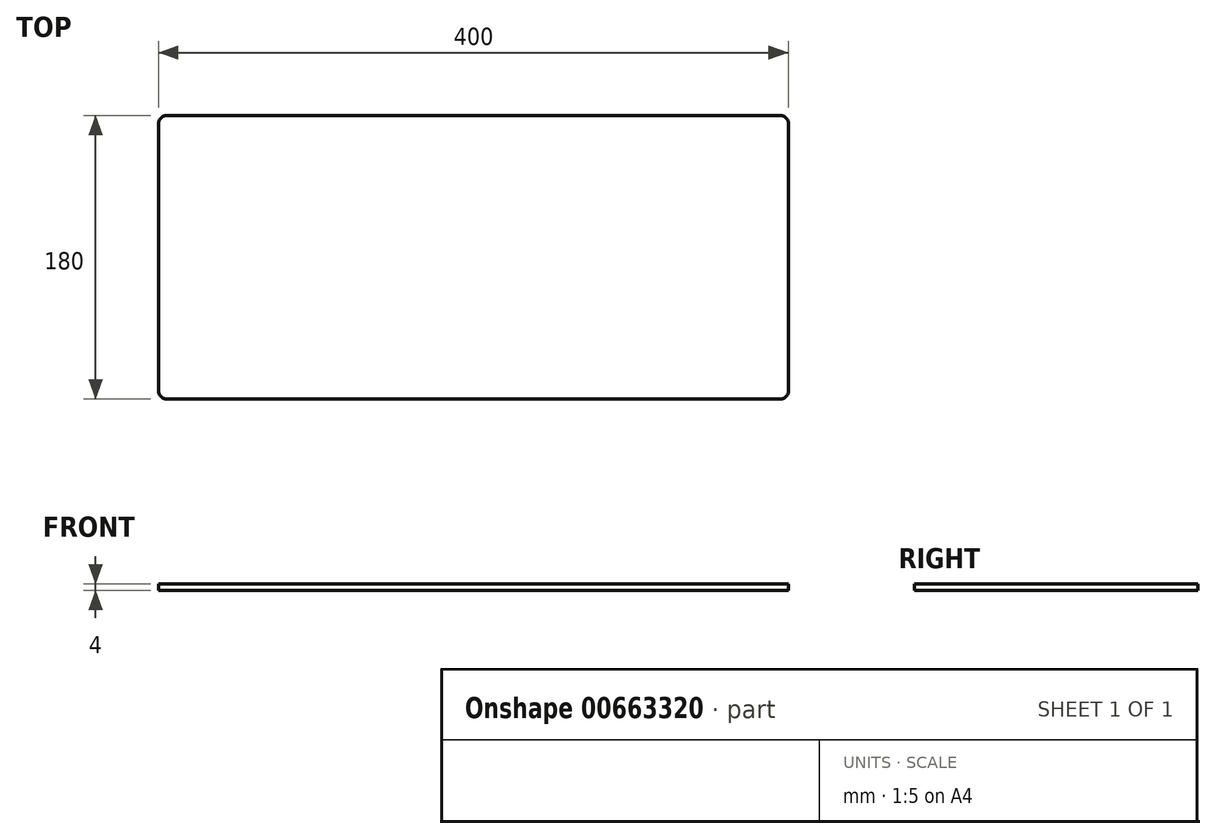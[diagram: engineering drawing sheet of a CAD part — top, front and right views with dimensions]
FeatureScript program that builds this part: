
annotation { "Feature Type Name" : "Feature", "Feature Type Description" : "" }
export const myFeature = defineFeature(function(context is Context, id is Id, definition is map)
    precondition{}
    {
        {
            var Q0;
            Q0=qCreatedBy(makeId("Top.planeOp"),FACE);
            var sketch = newSketch(context, id + "F0", { "sketchPlane" : qUnion([Q0])});
            skLineSegment(sketch, "E0.bottom", {"start": v(0, 0) * mm, "end": v(400, 0) * mm});
            skLineSegment(sketch, "E0.top", {"start": v(0, 180) * mm, "end": v(400, 180) * mm});
            skLineSegment(sketch, "E0.left", {"start": v(0, 0) * mm, "end": v(0, 180) * mm});
            skLineSegment(sketch, "E0.right", {"start": v(400, 0) * mm, "end": v(400, 180) * mm});
            skSolve(sketch);
        }
        {
            var Q0;
            Q0=makeQuery(id+"F0.imprint","IMPRINT",FACE,{"disambiguationData":[TD([[makeQuery(id+"F0.imprint","IMPRINT",EDGE,{"derivedFrom":sQuery(id+"F0.wireOp",EDGE,"E0.bottom")}),1.0]])]});
            extrude(context, id + "F1", {"entities" : qUnion([Q0]), "depth" : 4 * mm, "offsetDistance" : 25 * mm});
        }
        {
            var Q0;
            Q0=makeQuery(id+"F1.opExtrude","SWEPT_EDGE",EDGE,{"disambiguationData":[OSD([sQuery(id+"F0.wireOp",EDGE,"E0.top"),sQuery(id+"F0.wireOp",EDGE,"E0.left")])]});
            var Q1;
            Q1=makeQuery(id+"F1.opExtrude","SWEPT_EDGE",EDGE,{"disambiguationData":[OSD([sQuery(id+"F0.wireOp",EDGE,"E0.top"),sQuery(id+"F0.wireOp",EDGE,"E0.right")])]});
            var Q2;
            Q2=makeQuery(id+"F1.opExtrude","SWEPT_EDGE",EDGE,{"disambiguationData":[OSD([sQuery(id+"F0.wireOp",EDGE,"E0.bottom"),sQuery(id+"F0.wireOp",EDGE,"E0.right")])]});
            var Q3;
            Q3=makeQuery(id+"F1.opExtrude","SWEPT_EDGE",EDGE,{"disambiguationData":[OSD([sQuery(id+"F0.wireOp",EDGE,"E0.bottom"),sQuery(id+"F0.wireOp",EDGE,"E0.left")])]});
            fillet(context, id + "F2", {"entities" : qUnion([Q0, Q1, Q2, Q3]), "radius" : 5 * mm, "tangentPropagation" : true, "allowEdgeOverflow" : false});
        }
    });
